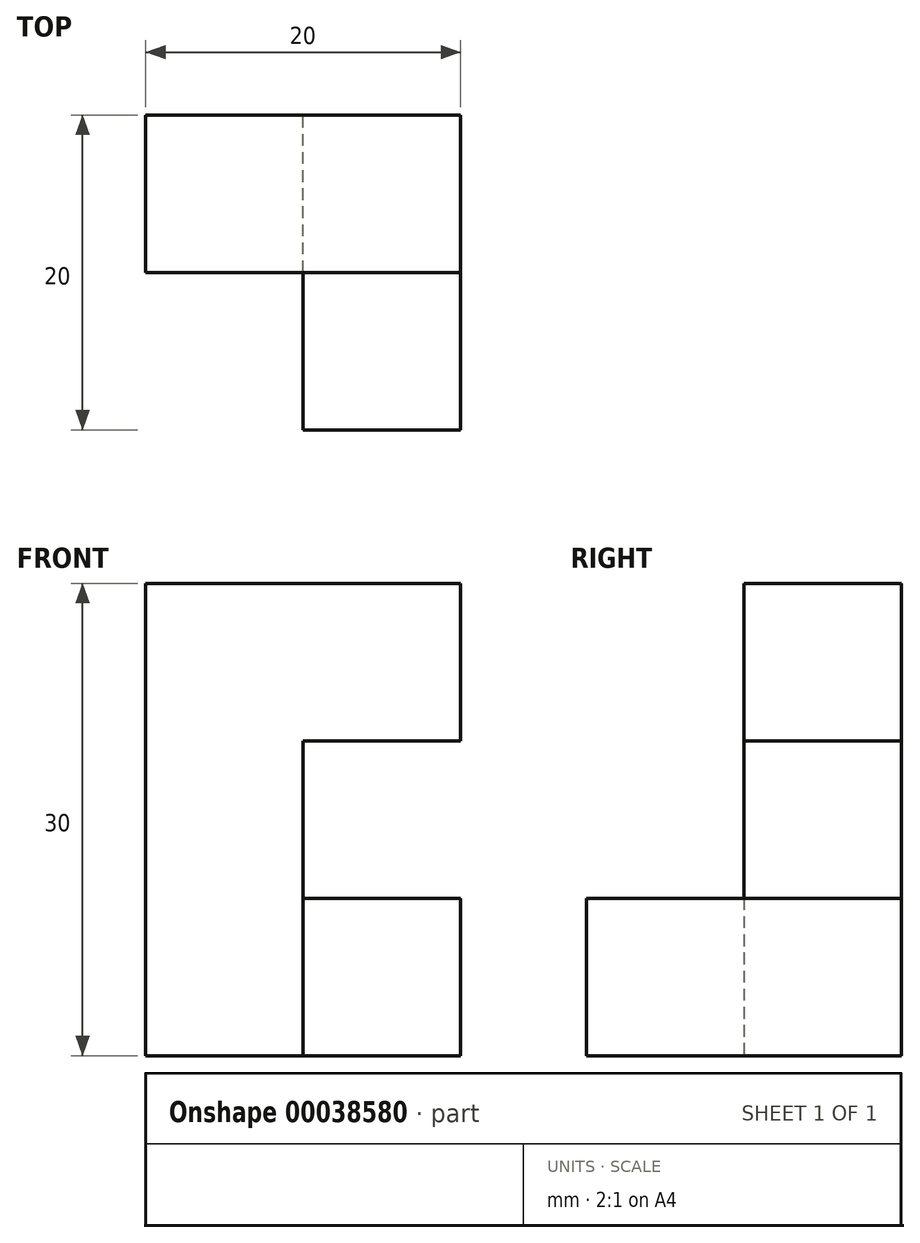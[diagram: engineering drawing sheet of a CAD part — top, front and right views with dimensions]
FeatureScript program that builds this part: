
annotation { "Feature Type Name" : "Feature", "Feature Type Description" : "" }
export const myFeature = defineFeature(function(context is Context, id is Id, definition is map)
    precondition{}
    {
        {
            var Q0;
            Q0=qCreatedBy(makeId("Top.planeOp"),FACE);
            var sketch = newSketch(context, id + "F0", { "sketchPlane" : qUnion([Q0])});
            skLineSegment(sketch, "E0.bottom", {"start": v(0, 0) * mm, "end": v(10, 0) * mm});
            skLineSegment(sketch, "E0.top", {"start": v(0, 10) * mm, "end": v(10, 10) * mm});
            skLineSegment(sketch, "E0.left", {"start": v(0, 0) * mm, "end": v(0, 10) * mm});
            skLineSegment(sketch, "E0.right", {"start": v(10, 0) * mm, "end": v(10, 10) * mm});
            skSolve(sketch);
        }
        {
            var Q0;
            Q0=makeQuery(id+"F0.imprint","IMPRINT",FACE,{"disambiguationData":[TD([[makeQuery(id+"F0.imprint","IMPRINT",EDGE,{"derivedFrom":sQuery(id+"F0.wireOp",EDGE,"E0.bottom")}),1.0]])]});
            extrude(context, id + "F1", {"entities" : qUnion([Q0]), "depth" : 30 * mm});
        }
        {
            var Q0;
            Q0=makeQuery(id+"F1.opExtrude","SWEPT_FACE",FACE,{"disambiguationData":[OSD([sQuery(id+"F0.wireOp",EDGE,"E0.right")])]});
            var sketch = newSketch(context, id + "F2", { "sketchPlane" : qUnion([Q0])});
            skLineSegment(sketch, "E1.bottom", {"start": v(0, 0) * mm, "end": v(10, 0) * mm});
            skLineSegment(sketch, "E1.top", {"start": v(0, 10) * mm, "end": v(10, 10) * mm});
            skLineSegment(sketch, "E1.left", {"start": v(0, 0) * mm, "end": v(0, 10) * mm});
            skLineSegment(sketch, "E1.right", {"start": v(10, 0) * mm, "end": v(10, 10) * mm});
            skSolve(sketch);
        }
        {
            var Q0;
            Q0=makeQuery(id+"F2.imprint","IMPRINT",FACE,{"disambiguationData":[TD([[makeQuery(id+"F2.imprint","IMPRINT",EDGE,{"derivedFrom":sQuery(id+"F2.wireOp",EDGE,"E1.bottom")}),1.0]])]});
            extrude(context, id + "F3", {"entities" : qUnion([Q0]), "operationType" : NewBodyOperationType.ADD, "depth" : 10 * mm});
        }
        {
            var Q0;
            Q0=makeQuery(id+"F3.boolean.opBoolean","MERGE",FACE,{"derivedFrom":[makeQuery(id+"F1.opExtrude","SWEPT_FACE",FACE,{"disambiguationData":[OSD([sQuery(id+"F0.wireOp",EDGE,"E0.bottom")])]}),makeQuery(id+"F3.opExtrude","SWEPT_FACE",FACE,{"disambiguationData":[OSD([sQuery(id+"F2.wireOp",EDGE,"E1.left")])]})]});
            var sketch = newSketch(context, id + "F4", { "sketchPlane" : qUnion([Q0])});
            skLineSegment(sketch, "E2.bottom", {"start": v(10, 10) * mm, "end": v(20, 10) * mm});
            skLineSegment(sketch, "E2.top", {"start": v(10, 0) * mm, "end": v(20, 0) * mm});
            skLineSegment(sketch, "E2.left", {"start": v(10, 10) * mm, "end": v(10, 0) * mm});
            skLineSegment(sketch, "E2.right", {"start": v(20, 10) * mm, "end": v(20, 0) * mm});
            skSolve(sketch);
        }
        {
            var Q0;
            Q0 = qSketchRegion(id + "F4", true);
            extrude(context, id + "F5", {"entities" : qUnion([Q0]), "operationType" : NewBodyOperationType.ADD, "depth" : 10 * mm});
        }
        {
            var Q0;
            Q0=makeQuery(id+"F1.opExtrude","SWEPT_FACE",FACE,{"disambiguationData":[OSD([sQuery(id+"F0.wireOp",EDGE,"E0.right")])]});
            var sketch = newSketch(context, id + "F6", { "sketchPlane" : qUnion([Q0])});
            skLineSegment(sketch, "E3.bottom", {"start": v(0, 30) * mm, "end": v(10, 30) * mm});
            skLineSegment(sketch, "E3.top", {"start": v(0, 20) * mm, "end": v(10, 20) * mm});
            skLineSegment(sketch, "E3.left", {"start": v(0, 30) * mm, "end": v(0, 20) * mm});
            skLineSegment(sketch, "E3.right", {"start": v(10, 30) * mm, "end": v(10, 20) * mm});
            skSolve(sketch);
        }
        {
            var Q0;
            Q0=makeQuery(id+"F6.imprint","IMPRINT",FACE,{"disambiguationData":[TD([[makeQuery(id+"F6.imprint","IMPRINT",EDGE,{"derivedFrom":sQuery(id+"F6.wireOp",EDGE,"E3.bottom")}),-1.0]])]});
            extrude(context, id + "F7", {"entities" : qUnion([Q0]), "operationType" : NewBodyOperationType.ADD, "depth" : 10 * mm});
        }
    });
